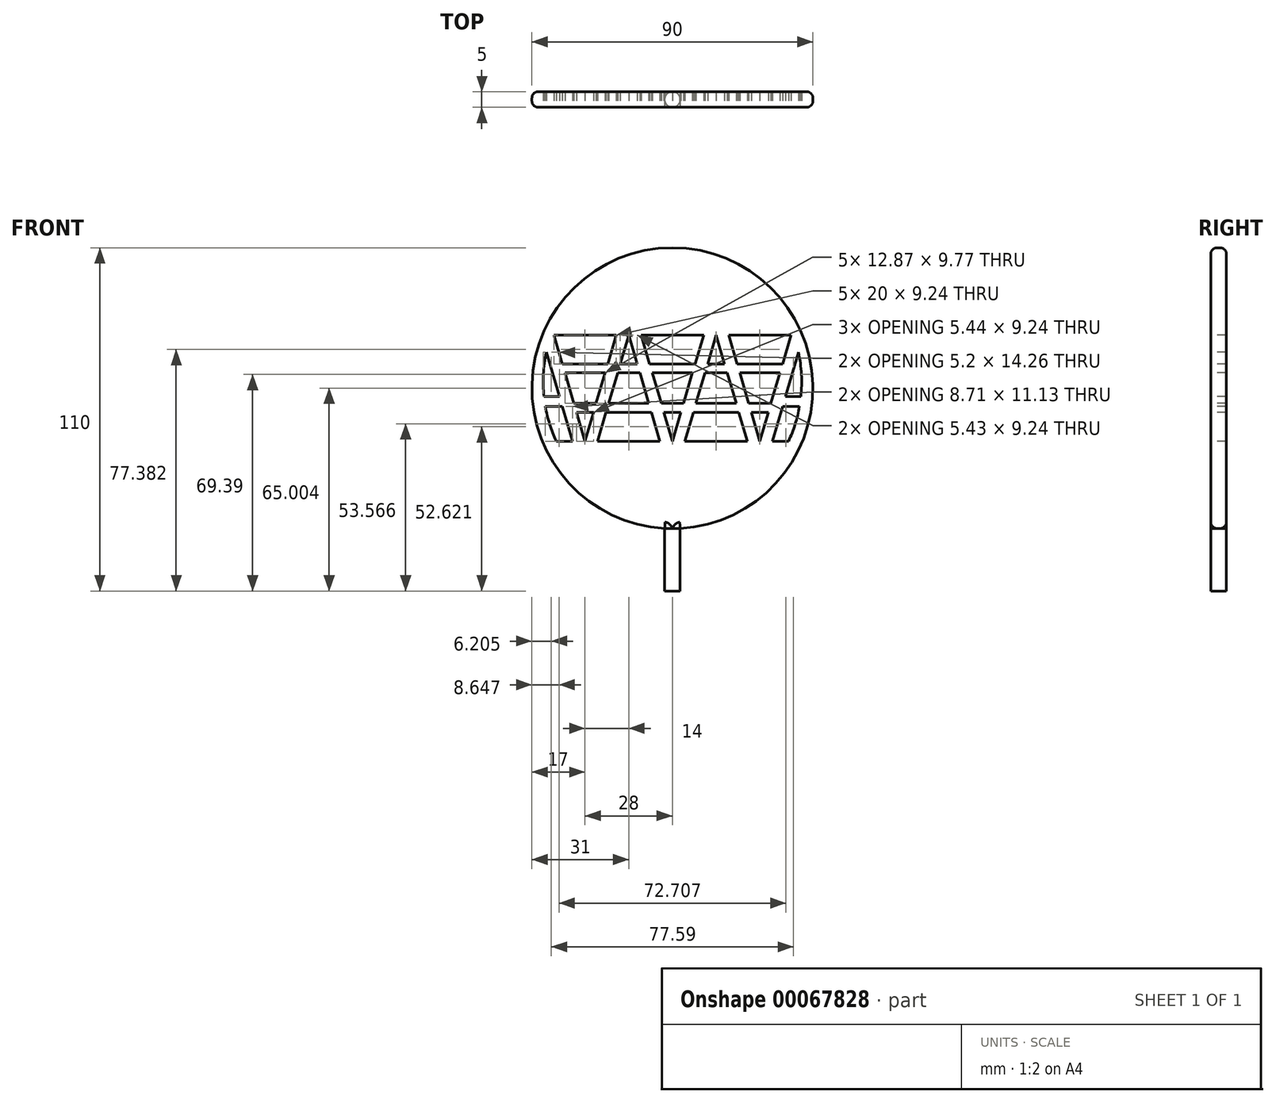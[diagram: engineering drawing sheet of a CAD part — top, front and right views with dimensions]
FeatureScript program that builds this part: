
annotation { "Feature Type Name" : "Feature", "Feature Type Description" : "" }
export const myFeature = defineFeature(function(context is Context, id is Id, definition is map)
    precondition{}
    {
        {
            var Q0;
            Q0=qCreatedBy(makeId("Front.planeOp"),FACE);
            var sketch = newSketch(context, id + "F0", { "sketchPlane" : qUnion([Q0])});
            skCircle(sketch, "E0", {"center": v(0, 0) * mm, "radius": 45 * mm});
            skSolve(sketch);
        }
        {
            var Q0;
            Q0=makeQuery(id+"F0.imprint","IMPRINT",FACE,{"disambiguationData":[TD([[makeQuery(id+"F0.imprint","IMPRINT",EDGE,{"derivedFrom":sQuery(id+"F0.wireOp",EDGE,"E0")}),1.0]])]});
            var Q1;
            Q1 = qSketchRegion(id + "F2", true);
            extrude(context, id + "F1", {"entities" : qUnion([Q0, Q1]), "depth" : 5 * mm});
        }
        {
            var Q0;
            Q0=qCreatedBy(makeId("Top.planeOp"),FACE);
            var sketch = newSketch(context, id + "F2", { "sketchPlane" : qUnion([Q0])});
            skCircle(sketch, "E1", {"center": v(0, -2.5) * mm, "radius": 2.5 * mm});
            skSolve(sketch);
        }
        {
            var Q0;
            Q0 = qSketchRegion(id + "F2", true);
            extrude(context, id + "F3", {"entities" : qUnion([Q0]), "operationType" : NewBodyOperationType.ADD, "oppositeDirection" : true, "depth" : 65 * mm});
        }
        {
            var Q0;
            Q0=makeQuery(id+"F1.opExtrude","CAP_EDGE",EDGE,{"disambiguationData":[OSD([sQuery(id+"F0.wireOp",EDGE,"E0")])],"isStart":false});
            fillet(context, id + "F4", {"entities" : qUnion([Q0]), "radius" : 2 * mm, "tangentPropagation" : true, "allowEdgeOverflow" : false});
        }
        {
            var Q0;
            Q0=makeQuery(id+"F1.opExtrude","CAP_EDGE",EDGE,{"disambiguationData":[OSD([sQuery(id+"F0.wireOp",EDGE,"E0")])],"isStart":true});
            fillet(context, id + "F5", {"entities" : qUnion([Q0]), "radius" : 2 * mm, "tangentPropagation" : true, "allowEdgeOverflow" : false});
        }
        {
            var Q0;
            Q0=makeQuery(id+"F1.opExtrude","CAP_FACE",FACE,{"disambiguationData":[OSD([sQuery(id+"F0.wireOp",EDGE,"E0")])],"isStart":false});
            var sketch = newSketch(context, id + "F6", { "sketchPlane" : qUnion([Q0])});
            skLineSegment(sketch, "E2", {"start": v(-39.5, 17) * mm, "end": v(0, 17) * mm, "construction": true});
            skLineSegment(sketch, "E3", {"start": v(0, 17) * mm, "end": v(39.5, 17) * mm, "construction": true});
            skLineSegment(sketch, "E4", {"start": v(-39.5, -17) * mm, "end": v(0, -17) * mm, "construction": true});
            skLineSegment(sketch, "E5", {"start": v(0, -17) * mm, "end": v(39.5, -17) * mm, "construction": true});
            skLineSegment(sketch, "E6", {"start": v(-10, 17) * mm, "end": v(0, -17) * mm});
            skLineSegment(sketch, "E7", {"start": v(0, 17) * mm, "end": v(-10, 17) * mm});
            skLineSegment(sketch, "E8", {"start": v(0, 17) * mm, "end": v(0, 0) * mm});
            skLineSegment(sketch, "E9", {"start": v(0, 0) * mm, "end": v(0, -17) * mm});
            skLineSegment(sketch, "E10", {"start": v(-14, 17) * mm, "end": v(-4, -17) * mm});
            skLineSegment(sketch, "E11", {"start": v(-4, -17) * mm, "end": v(-24, -17) * mm});
            skLineSegment(sketch, "E12", {"start": v(-24, -17) * mm, "end": v(-14, 17) * mm});
            skLineSegment(sketch, "E13", {"start": v(-18, 17) * mm, "end": v(-28, -17) * mm});
            skLineSegment(sketch, "E14", {"start": v(-28, -17) * mm, "end": v(-38, 17) * mm});
            skLineSegment(sketch, "E15", {"start": v(-38, 17) * mm, "end": v(-18, 17) * mm});
            skPoint(sketch, "E16.endSnap0", {"position": v(-33, 0) * mm});
            skLineSegment(sketch, "E17", {"start": v(-40.39, 11.52) * mm, "end": v(-32, -17) * mm});
            skLineSegment(sketch, "E18", {"start": v(-32, -17) * mm, "end": v(-37.2, -17) * mm});
            skArc(sketch, "E19", {"start": v(-40.39, 11.52) * mm, "mid": v(-41.12, -3) * mm, "end": v(-37.2, -17) * mm});
            skLineSegment(sketch, "E20", {"start": v(0, 17) * mm, "end": v(0, -17) * mm});
            skLineSegment(sketch, "E21.MirrorCS", {"start": v(10, 17) * mm, "end": v(0, -17) * mm});
            skLineSegment(sketch, "E22.MirrorCS", {"start": v(0, 17) * mm, "end": v(10, 17) * mm});
            skLineSegment(sketch, "E23.MirrorCS", {"start": v(14, 17) * mm, "end": v(4, -17) * mm});
            skLineSegment(sketch, "E24.MirrorCS", {"start": v(24, -17) * mm, "end": v(14, 17) * mm});
            skLineSegment(sketch, "E25.MirrorCS", {"start": v(4, -17) * mm, "end": v(24, -17) * mm});
            skLineSegment(sketch, "E26.MirrorCS", {"start": v(28, -17) * mm, "end": v(38, 17) * mm});
            skLineSegment(sketch, "E27.MirrorCS", {"start": v(18, 17) * mm, "end": v(28, -17) * mm});
            skLineSegment(sketch, "E28.MirrorCS", {"start": v(38, 17) * mm, "end": v(18, 17) * mm});
            skLineSegment(sketch, "E29.MirrorCS", {"start": v(40.39, 11.52) * mm, "end": v(32, -17) * mm});
            skArc(sketch, "E30.MirrorCS", {"start": v(40.39, 11.52) * mm, "mid": v(41.12, -3) * mm, "end": v(37.2, -17) * mm});
            skLineSegment(sketch, "E31.MirrorCS", {"start": v(32, -17) * mm, "end": v(37.2, -17) * mm});
            skPoint(sketch, "E32.startSnap0", {"position": v(33, 0) * mm});
            skPoint(sketch, "E33.startSnap0", {"position": v(-36.2, -2.74) * mm});
            skPoint(sketch, "E33.endSnap0", {"position": v(0, -8.5) * mm});
            skPoint(sketch, "E34.endSnap0", {"position": v(-9, 0) * mm});
            skLineSegment(sketch, "E35", {"start": v(-35.28, 7.76) * mm, "end": v(0, 7.76) * mm, "construction": true});
            skPoint(sketch, "E35.endSnap0", {"position": v(0, 8.5) * mm});
            skLineSegment(sketch, "E36", {"start": v(-34.44, 4.89) * mm, "end": v(0, 4.89) * mm, "construction": true});
            skLineSegment(sketch, "E37", {"start": v(-31.57, -4.88) * mm, "end": v(0, -4.88) * mm, "construction": true});
            skLineSegment(sketch, "E38", {"start": v(-30.72, -7.76) * mm, "end": v(0, -7.76) * mm, "construction": true});
            skLineSegment(sketch, "E39", {"start": v(-36.2, -2.74) * mm, "end": v(-41.15, -2.74) * mm});
            skLineSegment(sketch, "E40", {"start": v(-35.27, -5.87) * mm, "end": v(-40.7, -5.87) * mm});
            skLineSegment(sketch, "E41", {"start": v(-35.28, 7.76) * mm, "end": v(-20.72, 7.76) * mm});
            skLineSegment(sketch, "E42", {"start": v(-34.44, 4.89) * mm, "end": v(-21.56, 4.89) * mm});
            skLineSegment(sketch, "E43", {"start": v(-31.57, -4.88) * mm, "end": v(-24.43, -4.88) * mm});
            skLineSegment(sketch, "E44", {"start": v(-30.72, -7.76) * mm, "end": v(-25.28, -7.76) * mm});
            skLineSegment(sketch, "E45", {"start": v(-16.72, 7.76) * mm, "end": v(-11.28, 7.76) * mm});
            skLineSegment(sketch, "E46", {"start": v(-17.56, 4.89) * mm, "end": v(-10.44, 4.89) * mm});
            skPoint(sketch, "E46.startSnap0", {"position": v(-17.22, 4.89) * mm});
            skLineSegment(sketch, "E47", {"start": v(-20.43, -4.88) * mm, "end": v(-7.57, -4.88) * mm});
            skLineSegment(sketch, "E48", {"start": v(-21.28, -7.76) * mm, "end": v(-6.72, -7.76) * mm});
            skLineSegment(sketch, "E49", {"start": v(-7.28, 7.76) * mm, "end": v(0, 7.76) * mm});
            skLineSegment(sketch, "E50", {"start": v(-6.44, 4.89) * mm, "end": v(0, 4.89) * mm});
            skLineSegment(sketch, "E51", {"start": v(-3.57, -4.88) * mm, "end": v(0, -4.88) * mm});
            skLineSegment(sketch, "E52", {"start": v(-2.72, -7.76) * mm, "end": v(0, -7.76) * mm});
            skLineSegment(sketch, "E53.MirrorCS", {"start": v(7.28, 7.76) * mm, "end": v(0, 7.76) * mm});
            skLineSegment(sketch, "E54.MirrorCS", {"start": v(6.44, 4.89) * mm, "end": v(0, 4.89) * mm});
            skLineSegment(sketch, "E55.MirrorCS", {"start": v(3.57, -4.88) * mm, "end": v(0, -4.88) * mm});
            skLineSegment(sketch, "E56.MirrorCS", {"start": v(20.43, -4.88) * mm, "end": v(7.57, -4.88) * mm});
            skLineSegment(sketch, "E57.MirrorCS", {"start": v(21.28, -7.76) * mm, "end": v(6.72, -7.76) * mm});
            skLineSegment(sketch, "E58.MirrorCS", {"start": v(17.56, 4.89) * mm, "end": v(10.44, 4.89) * mm});
            skLineSegment(sketch, "E59.MirrorCS", {"start": v(16.72, 7.76) * mm, "end": v(11.28, 7.76) * mm});
            skLineSegment(sketch, "E60.MirrorCS", {"start": v(35.28, 7.76) * mm, "end": v(20.72, 7.76) * mm});
            skLineSegment(sketch, "E61.MirrorCS", {"start": v(34.44, 4.89) * mm, "end": v(21.56, 4.89) * mm});
            skLineSegment(sketch, "E62.MirrorCS", {"start": v(31.57, -4.88) * mm, "end": v(24.43, -4.88) * mm});
            skLineSegment(sketch, "E63.MirrorCS", {"start": v(30.72, -7.76) * mm, "end": v(25.28, -7.76) * mm});
            skLineSegment(sketch, "E64.MirrorCS", {"start": v(35.27, -5.87) * mm, "end": v(40.7, -5.87) * mm});
            skPoint(sketch, "E65.MirrorP", {"position": v(36.2, -2.74) * mm});
            skLineSegment(sketch, "E66.MirrorCS", {"start": v(36.2, -2.74) * mm, "end": v(41.15, -2.74) * mm});
            skLineSegment(sketch, "E67.MirrorCS", {"start": v(2.72, -7.76) * mm, "end": v(0, -7.76) * mm});
            skSolve(sketch);
        }
        {
            var Q0;
            {var subQ0=sQuery(id+"F6.wireOp",EDGE,"E15");Q0=makeQuery(id+"F6.imprint","IMPRINT",FACE,{"disambiguationData":[TD([[makeQuery(id+"F6.imprint","IMPRINT",EDGE,{"derivedFrom":subQ0}),-1.0]])]});}
            var Q1;
            {var subQ3=sQuery(id+"F6.wireOp",EDGE,"E39");Q1=makeQuery(id+"F6.imprint","IMPRINT",FACE,{"disambiguationData":[TD([[makeQuery(id+"F6.imprint","IMPRINT",EDGE,{"derivedFrom":subQ3}),-1.0]])]});}
            var Q2;
            {var subQ0=sQuery(id+"F6.wireOp",EDGE,"E18");Q2=makeQuery(id+"F6.imprint","IMPRINT",FACE,{"disambiguationData":[TD([[makeQuery(id+"F6.imprint","IMPRINT",EDGE,{"derivedFrom":subQ0}),-1.0]])]});}
            var Q3;
            {var subQ0=sQuery(id+"F6.wireOp",EDGE,"E42");Q3=makeQuery(id+"F6.imprint","IMPRINT",FACE,{"disambiguationData":[TD([[makeQuery(id+"F6.imprint","IMPRINT",EDGE,{"derivedFrom":subQ0}),-1.0]])]});}
            var Q4;
            {var subQ3=sQuery(id+"F6.wireOp",EDGE,"E44");Q4=makeQuery(id+"F6.imprint","IMPRINT",FACE,{"disambiguationData":[TD([[makeQuery(id+"F6.imprint","IMPRINT",EDGE,{"derivedFrom":subQ3}),-1.0]])]});}
            var Q5;
            {var subQ3=sQuery(id+"F6.wireOp",EDGE,"E45");Q5=makeQuery(id+"F6.imprint","IMPRINT",FACE,{"disambiguationData":[TD([[makeQuery(id+"F6.imprint","IMPRINT",EDGE,{"derivedFrom":subQ3}),1.0]])]});}
            var Q6;
            {var subQ0=sQuery(id+"F6.wireOp",EDGE,"E46");Q6=makeQuery(id+"F6.imprint","IMPRINT",FACE,{"disambiguationData":[TD([[makeQuery(id+"F6.imprint","IMPRINT",EDGE,{"derivedFrom":subQ0}),-1.0]])]});}
            var Q7;
            {var subQ0=sQuery(id+"F6.wireOp",EDGE,"E11");Q7=makeQuery(id+"F6.imprint","IMPRINT",FACE,{"disambiguationData":[TD([[makeQuery(id+"F6.imprint","IMPRINT",EDGE,{"derivedFrom":subQ0}),-1.0]])]});}
            var Q8;
            {var subQ1=sQuery(id+"F6.wireOp",EDGE,"E6");var subQ3=sQuery(id+"F6.wireOp",EDGE,"E52");var subQ4=makeQuery(id+"F6.imprint","INTERSECT",VERTEX,{"derivedFrom":[subQ1,subQ3]});Q8=makeQuery(id+"F6.imprint","IMPRINT",FACE,{"disambiguationData":[TD([[makeQuery(id+"F6.imprint","IMPRINT",EDGE,{"disambiguationData":[TD([[subQ4,-1.0]])],"derivedFrom":subQ1}),1.0]])]});}
            var Q9;
            {var subQ0=sQuery(id+"F6.wireOp",EDGE,"E21.MirrorCS");var subQ3=sQuery(id+"F6.wireOp",EDGE,"E67.MirrorCS");var subQ5=makeQuery(id+"F6.imprint","INTERSECT",VERTEX,{"derivedFrom":[subQ0,subQ3]});Q9=makeQuery(id+"F6.imprint","IMPRINT",FACE,{"disambiguationData":[TD([[makeQuery(id+"F6.imprint","IMPRINT",EDGE,{"disambiguationData":[TD([[subQ5,-1.0]])],"derivedFrom":subQ0}),-1.0]])]});}
            var Q10;
            {var subQ0=sQuery(id+"F6.wireOp",EDGE,"E54.MirrorCS");Q10=makeQuery(id+"F6.imprint","IMPRINT",FACE,{"disambiguationData":[TD([[makeQuery(id+"F6.imprint","IMPRINT",EDGE,{"derivedFrom":subQ0}),1.0]])]});}
            var Q11;
            {var subQ3=sQuery(id+"F6.wireOp",EDGE,"E50");Q11=makeQuery(id+"F6.imprint","IMPRINT",FACE,{"disambiguationData":[TD([[makeQuery(id+"F6.imprint","IMPRINT",EDGE,{"derivedFrom":subQ3}),-1.0]])]});}
            var Q12;
            {var subQ0=sQuery(id+"F6.wireOp",EDGE,"E7");Q12=makeQuery(id+"F6.imprint","IMPRINT",FACE,{"disambiguationData":[TD([[makeQuery(id+"F6.imprint","IMPRINT",EDGE,{"derivedFrom":subQ0}),1.0]])]});}
            var Q13;
            {var subQ0=sQuery(id+"F6.wireOp",EDGE,"E22.MirrorCS");Q13=makeQuery(id+"F6.imprint","IMPRINT",FACE,{"disambiguationData":[TD([[makeQuery(id+"F6.imprint","IMPRINT",EDGE,{"derivedFrom":subQ0}),-1.0]])]});}
            var Q14;
            {var subQ3=sQuery(id+"F6.wireOp",EDGE,"E59.MirrorCS");Q14=makeQuery(id+"F6.imprint","IMPRINT",FACE,{"disambiguationData":[TD([[makeQuery(id+"F6.imprint","IMPRINT",EDGE,{"derivedFrom":subQ3}),-1.0]])]});}
            var Q15;
            {var subQ0=sQuery(id+"F6.wireOp",EDGE,"E56.MirrorCS");Q15=makeQuery(id+"F6.imprint","IMPRINT",FACE,{"disambiguationData":[TD([[makeQuery(id+"F6.imprint","IMPRINT",EDGE,{"derivedFrom":subQ0}),-1.0]])]});}
            var Q16;
            {var subQ0=sQuery(id+"F6.wireOp",EDGE,"E25.MirrorCS");Q16=makeQuery(id+"F6.imprint","IMPRINT",FACE,{"disambiguationData":[TD([[makeQuery(id+"F6.imprint","IMPRINT",EDGE,{"derivedFrom":subQ0}),1.0]])]});}
            var Q17;
            {var subQ3=sQuery(id+"F6.wireOp",EDGE,"E63.MirrorCS");Q17=makeQuery(id+"F6.imprint","IMPRINT",FACE,{"disambiguationData":[TD([[makeQuery(id+"F6.imprint","IMPRINT",EDGE,{"derivedFrom":subQ3}),1.0]])]});}
            var Q18;
            {var subQ0=sQuery(id+"F6.wireOp",EDGE,"E61.MirrorCS");Q18=makeQuery(id+"F6.imprint","IMPRINT",FACE,{"disambiguationData":[TD([[makeQuery(id+"F6.imprint","IMPRINT",EDGE,{"derivedFrom":subQ0}),1.0]])]});}
            var Q19;
            {var subQ0=sQuery(id+"F6.wireOp",EDGE,"E28.MirrorCS");Q19=makeQuery(id+"F6.imprint","IMPRINT",FACE,{"disambiguationData":[TD([[makeQuery(id+"F6.imprint","IMPRINT",EDGE,{"derivedFrom":subQ0}),1.0]])]});}
            var Q20;
            {var subQ3=sQuery(id+"F6.wireOp",EDGE,"E66.MirrorCS");Q20=makeQuery(id+"F6.imprint","IMPRINT",FACE,{"disambiguationData":[TD([[makeQuery(id+"F6.imprint","IMPRINT",EDGE,{"derivedFrom":subQ3}),1.0]])]});}
            var Q21;
            {var subQ0=sQuery(id+"F6.wireOp",EDGE,"E31.MirrorCS");Q21=makeQuery(id+"F6.imprint","IMPRINT",FACE,{"disambiguationData":[TD([[makeQuery(id+"F6.imprint","IMPRINT",EDGE,{"derivedFrom":subQ0}),1.0]])]});}
            extrude(context, id + "F7", {"entities" : qUnion([Q0, Q1, Q2, Q3, Q4, Q5, Q6, Q7, Q8, Q9, Q10, Q11, Q12, Q13, Q14, Q15, Q16, Q17, Q18, Q19, Q20, Q21]), "operationType" : NewBodyOperationType.REMOVE, "endBound" : BoundingType.THROUGH_ALL, "oppositeDirection" : true, "depth" : 25 * mm});
        }
    });
